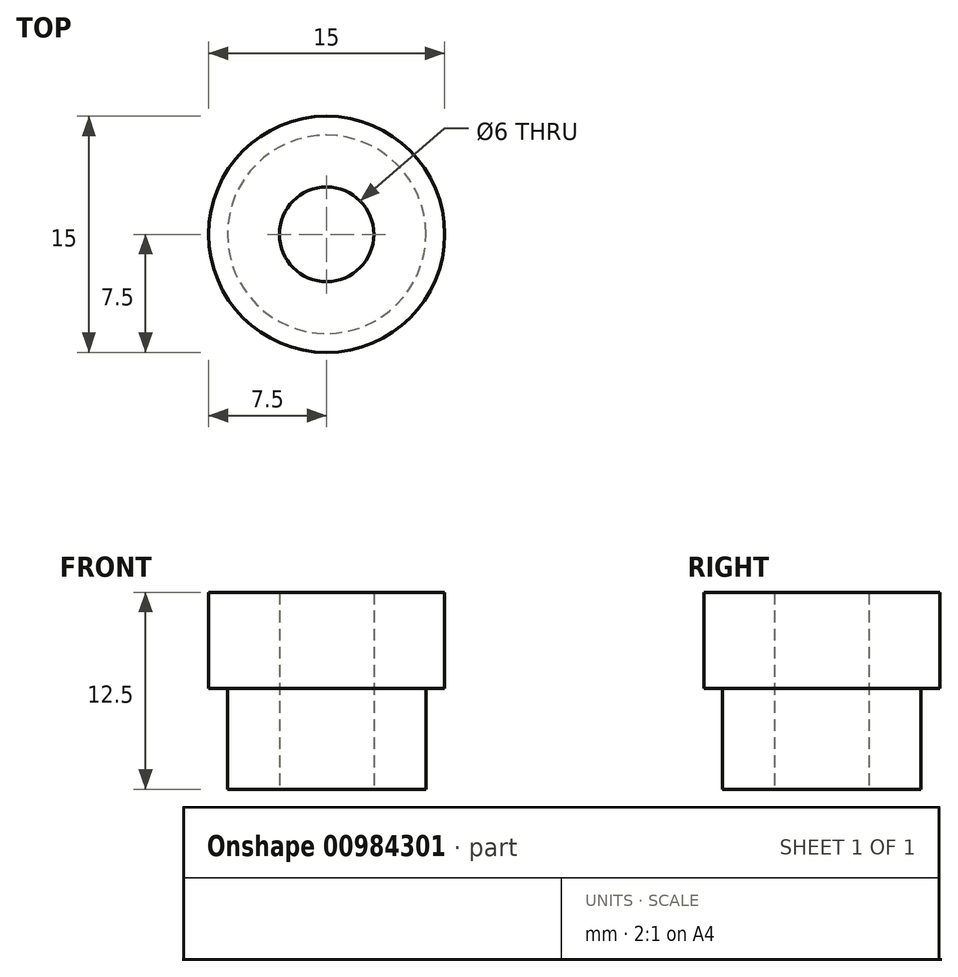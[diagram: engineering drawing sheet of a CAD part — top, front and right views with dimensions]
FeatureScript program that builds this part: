
annotation { "Feature Type Name" : "Feature", "Feature Type Description" : "" }
export const myFeature = defineFeature(function(context is Context, id is Id, definition is map)
    precondition{}
    {
        {
            var Q0;
            Q0=qCreatedBy(makeId("Top.planeOp"),FACE);
            var sketch = newSketch(context, id + "F0", { "sketchPlane" : qUnion([Q0])});
            skCircle(sketch, "E0", {"center": v(0, 0) * mm, "radius": 7.5 * mm});
            skCircle(sketch, "E1", {"center": v(0, 0) * mm, "radius": 3 * mm});
            skSolve(sketch);
        }
        {
            var Q0;
            Q0=qSketchRegion(id+"F0",true);
            extrude(context, id + "F1", {"entities" : qUnion([Q0]), "depth" : 12.5 * mm, "offsetDistance" : 25 * mm});
        }
        {
            var Q0;
            Q0=qCreatedBy(makeId("Top.planeOp"),FACE);
            var sketch = newSketch(context, id + "F2", { "sketchPlane" : qUnion([Q0])});
            skCircle(sketch, "E2", {"center": v(0, 0) * mm, "radius": 6.3 * mm});
            skCircle(sketch, "E3.0", {"center": v(0, 0) * mm, "radius": 7.5 * mm});
            skSolve(sketch);
        }
        {
            var Q0;
            Q0=qSketchRegion(id+"F2",true);
            extrude(context, id + "F3", {"entities" : qUnion([Q0]), "operationType" : NewBodyOperationType.REMOVE, "depth" : (12.8 / 2) * mm, "offsetDistance" : 25 * mm});
        }
    });
